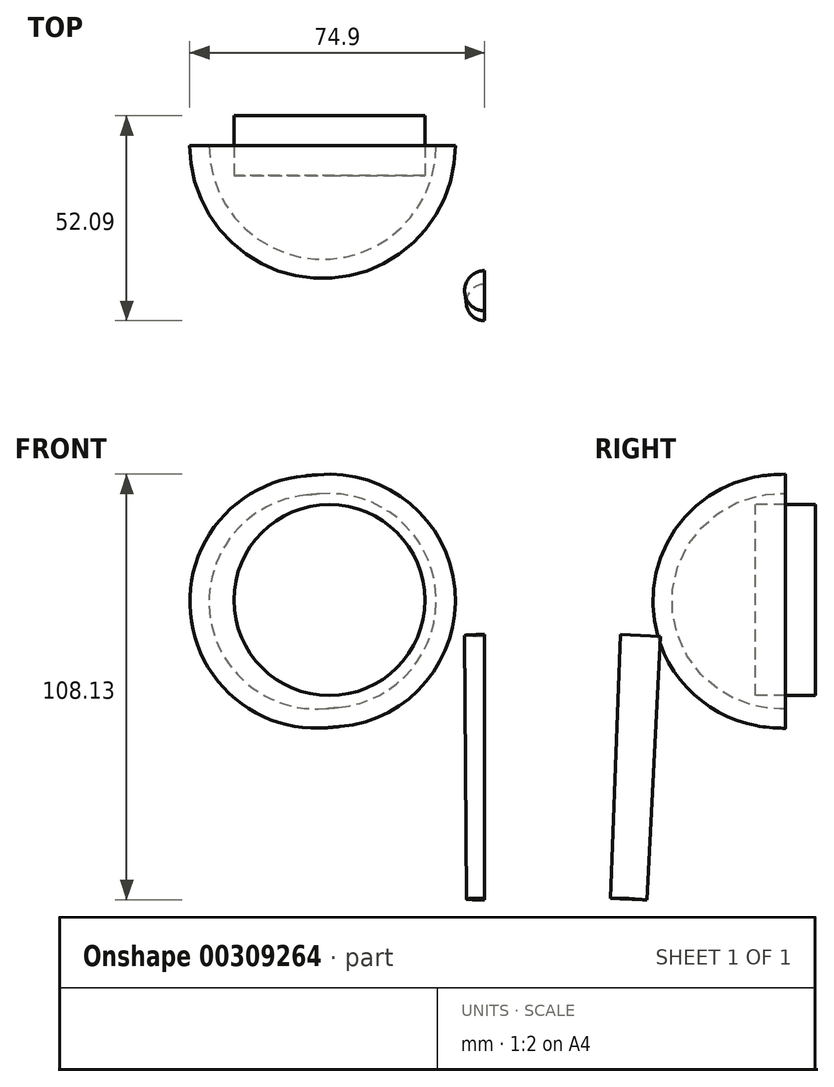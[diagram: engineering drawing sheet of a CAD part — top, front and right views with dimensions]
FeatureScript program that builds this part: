
annotation { "Feature Type Name" : "Feature", "Feature Type Description" : "" }
export const myFeature = defineFeature(function(context is Context, id is Id, definition is map)
    precondition{}
    {
        {
            var Q0;
            Q0=qCreatedBy(makeId("Front.planeOp"),FACE);
            var sketch = newSketch(context, id + "F0", { "sketchPlane" : qUnion([Q0])});
            skArc(sketch, "E0", {"start": v(-38.28, 8.35) * mm, "mid": v(-7.55, 43.32) * mm, "end": v(-44.04, 72.24) * mm});
            skLineSegment(sketch, "E1", {"start": v(-44.04, 72.24) * mm, "end": v(-38.28, 8.35) * mm});
            skArc(sketch, "E2", {"start": v(-43.6, 67.36) * mm, "mid": v(-12.42, 42.88) * mm, "end": v(-38.72, 13.23) * mm});
            skSolve(sketch);
        }
        {
            var Q0;
            Q0=makeQuery(id+"F0.imprint","IMPRINT",FACE,{"disambiguationData":[TD([[makeQuery(id+"F0.imprint","IMPRINT",EDGE,{"derivedFrom":sQuery(id+"F0.wireOp",EDGE,"E0")}),1.0]])]});
            var Q1;
            Q1=sQuery(id+"F0.wireOp",EDGE,"E1");
            revolve(context, id + "F1", {"entities" : qUnion([Q0]), "axis" : qUnion([Q1]), "revolveType" : RevolveType.ONE_DIRECTION, "angle" : 180 * degree});
        }
        {
            var Q0;
            Q0=qCreatedBy(makeId("Right.planeOp"),FACE);
            var sketch = newSketch(context, id + "F2", { "sketchPlane" : qUnion([Q0])});
            skLineSegment(sketch, "E3", {"start": v(-41.95, 31.8) * mm, "end": v(-44.47, -35.16) * mm});
            skLineSegment(sketch, "E4", {"start": v(-36.85, 31.62) * mm, "end": v(-39.81, -35.16) * mm});
            skLineSegment(sketch, "E5", {"start": v(-36.85, 31.62) * mm, "end": v(-41.95, 31.8) * mm});
            skLineSegment(sketch, "E6", {"start": v(-39.81, -35.16) * mm, "end": v(-44.47, -35.16) * mm});
            skSolve(sketch);
        }
        {
            var Q0;
            Q0=makeQuery(id+"F2.imprint","IMPRINT",FACE,{"disambiguationData":[TD([[makeQuery(id+"F2.imprint","IMPRINT",EDGE,{"derivedFrom":sQuery(id+"F2.wireOp",EDGE,"E3")}),1.0]])]});
            var Q1;
            Q1=sQuery(id+"F2.wireOp",EDGE,"E4");
            revolve(context, id + "F3", {"entities" : qUnion([Q0]), "axis" : qUnion([Q1]), "revolveType" : RevolveType.ONE_DIRECTION, "angle" : 180 * degree});
        }
        {
            var Q0;
            Q0=qCreatedBy(makeId("Front.planeOp"),FACE);
            var sketch = newSketch(context, id + "F4", { "sketchPlane" : qUnion([Q0])});
            skCircle(sketch, "E7", {"center": v(-39.43, 40.58) * mm, "radius": 24.27 * mm});
            skSolve(sketch);
        }
        {
            var Q0;
            Q0=makeQuery(id+"F4.imprint","IMPRINT",FACE,{"disambiguationData":[TD([[makeQuery(id+"F4.imprint","IMPRINT",EDGE,{"derivedFrom":sQuery(id+"F4.wireOp",EDGE,"E7")}),1.0]])]});
            extrude(context, id + "F5", {"entities" : qUnion([Q0]), "endBound" : BoundingType.SYMMETRIC, "oppositeDirection" : true, "depth" : 15.24 * mm});
        }
    });
